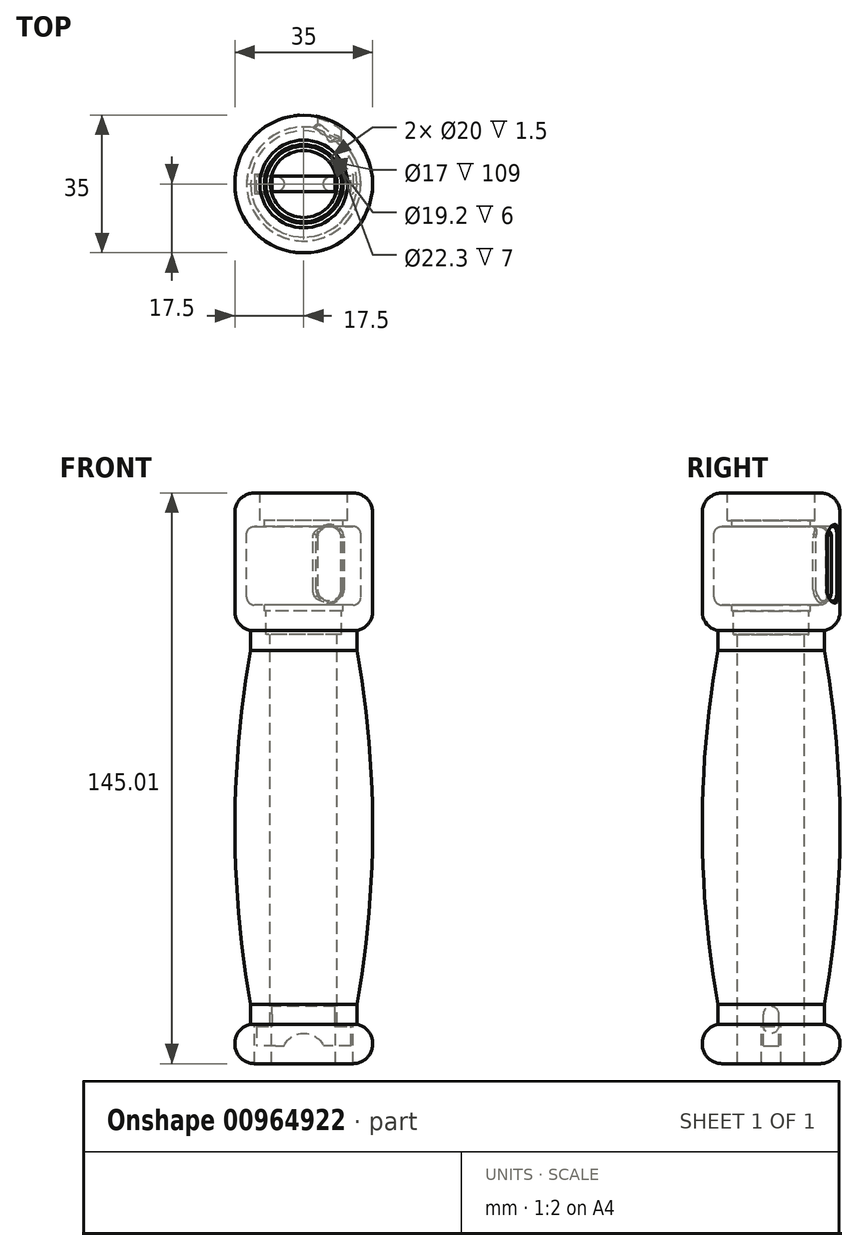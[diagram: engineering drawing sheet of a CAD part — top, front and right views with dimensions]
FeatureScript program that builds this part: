
annotation { "Feature Type Name" : "Feature", "Feature Type Description" : "" }
export const myFeature = defineFeature(function(context is Context, id is Id, definition is map)
    precondition{}
    {
        {
            var Q0;
            Q0=qCreatedBy(makeId("Front.planeOp"),FACE);
            var sketch = newSketch(context, id + "F0", { "sketchPlane" : qUnion([Q0])});
            skLineSegment(sketch, "E0", {"start": v(0, 0) * mm, "end": v(0, -145) * mm, "construction": true});
            skLineSegment(sketch, "E1", {"start": v(-17.5, 0) * mm, "end": v(-17.5, -35) * mm});
            skLineSegment(sketch, "E2", {"start": v(-17.5, -35) * mm, "end": v(-13.5, -35) * mm});
            skLineSegment(sketch, "E3", {"start": v(-13.5, -35) * mm, "end": v(-13.5, -40) * mm});
            skLineSegment(sketch, "E4", {"start": v(-13.5, -135) * mm, "end": v(-17.5, -135) * mm});
            skLineSegment(sketch, "E5", {"start": v(-17.5, -135) * mm, "end": v(-17.5, -145) * mm});
            skLineSegment(sketch, "E6", {"start": v(-17.5, 0) * mm, "end": v(-11.15, 0) * mm});
            skLineSegment(sketch, "E7", {"start": v(-11.15, 0) * mm, "end": v(0, 0) * mm, "construction": true});
            skLineSegment(sketch, "E8", {"start": v(-11.15, 0) * mm, "end": v(-11.15, -7) * mm});
            skLineSegment(sketch, "E9", {"start": v(-11.15, -7) * mm, "end": v(-10, -7) * mm});
            skLineSegment(sketch, "E10", {"start": v(-10, -7) * mm, "end": v(-10, -8.5) * mm});
            skLineSegment(sketch, "E11", {"start": v(-10, -30) * mm, "end": v(-9.6, -30) * mm});
            skLineSegment(sketch, "E12", {"start": v(-9.6, -30) * mm, "end": v(-9.6, -36) * mm});
            skLineSegment(sketch, "E13", {"start": v(-9.6, -36) * mm, "end": v(-8.5, -36) * mm});
            skLineSegment(sketch, "E14", {"start": v(-8.5, -36) * mm, "end": v(-8.5, -145) * mm});
            skLineSegment(sketch, "E15", {"start": v(-17.5, -145) * mm, "end": v(-8.5, -145) * mm});
            skLineSegment(sketch, "E16", {"start": v(-8.5, -145) * mm, "end": v(0, -145) * mm, "construction": true});
            skArc(sketch, "E17", {"start": v(-13.5, -40) * mm, "mid": v(-17.5, -85) * mm, "end": v(-13.5, -130) * mm});
            skLineSegment(sketch, "E18.trimOffspring", {"start": v(-13.5, -130) * mm, "end": v(-13.5, -135) * mm});
            skLineSegment(sketch, "E19", {"start": v(-13.5, -130) * mm, "end": v(-13.5, -40) * mm, "construction": true});
            skLineSegment(sketch, "E20", {"start": v(-10, -8.5) * mm, "end": v(-12.5, -8.5) * mm});
            skLineSegment(sketch, "E21", {"start": v(-14.5, -10.5) * mm, "end": v(-14.5, -26.5) * mm});
            skLineSegment(sketch, "E22", {"start": v(-12.5, -28.5) * mm, "end": v(-10, -28.5) * mm});
            skLineSegment(sketch, "E23.trimOffspring", {"start": v(-10, -28.5) * mm, "end": v(-10, -30) * mm});
            skPoint(sketch, "E24.visualSharp", {"position": v(-14.5, -8.5) * mm});
            skArc(sketch, "E24.filletArc", {"start": v(-12.5, -8.5) * mm, "mid": v(-13.91, -9.09) * mm, "end": v(-14.5, -10.5) * mm});
            skPoint(sketch, "E25.visualSharp", {"position": v(-14.5, -28.5) * mm});
            skArc(sketch, "E25.filletArc", {"start": v(-14.5, -26.5) * mm, "mid": v(-13.91, -27.91) * mm, "end": v(-12.5, -28.5) * mm});
            skSolve(sketch);
        }
        {
            var Q0;
            Q0 = qSketchRegion(id + "F0", true);
            var Q1;
            Q1=sQuery(id+"F0.wireOp",EDGE,"E0");
            revolve(context, id + "F1", {"surfaceOperationType" : NewSurfaceOperationType.NEW, "entities" : qUnion([Q0]), "axis" : qUnion([Q1]), "revolveType" : RevolveType.FULL});
        }
        {
            var Q0;
            Q0=qCreatedBy(makeId("Front.planeOp"),FACE);
            var sketch = newSketch(context, id + "F2", { "sketchPlane" : qUnion([Q0])});
            skLineSegment(sketch, "E26", {"start": v(0, 0) * mm, "end": v(0, -17) * mm, "construction": true});
            skLineSegment(sketch, "E27", {"start": v(6.5, -11.5) * mm, "end": v(6.5, -24.5) * mm, "construction": true});
            skLineSegment(sketch, "E28.0", {"start": v(3.5, -11.5) * mm, "end": v(3.5, -24.5) * mm});
            skLineSegment(sketch, "E29.0", {"start": v(9.5, -11.5) * mm, "end": v(9.5, -24.5) * mm});
            skArc(sketch, "E30", {"start": v(9.5, -11.5) * mm, "mid": v(6.5, -8.5) * mm, "end": v(3.5, -11.5) * mm});
            skArc(sketch, "E31", {"start": v(3.5, -24.5) * mm, "mid": v(6.5, -27.5) * mm, "end": v(9.5, -24.5) * mm});
            skSolve(sketch);
        }
        {
            var Q0;
            Q0 = qSketchRegion(id + "F2", true);
            var Q1;
            Q1=makeQuery(id+"F1.opRevolve","SWEPT_FACE",FACE,{"disambiguationData":[OSD([sQuery(id+"F0.wireOp",EDGE,"E17")])]});
            extrude(context, id + "F3", {"entities" : qUnion([Q0]), "operationType" : NewBodyOperationType.REMOVE, "oppositeDirection" : true, "depth" : 25 * mm, "endBoundEntityFace" : qUnion([Q1]), "offsetDistance" : 25 * mm});
        }
        {
            var Q0;
            Q0=makeQuery(id+"FU2xquRf8RpkaLV_1.boolean.opBoolean","INTERSECT",EDGE,{"derivedFrom":[makeQuery(id+"F3.boolean.opBoolean","COPY",FACE,{"derivedFrom":makeQuery(id+"F3.opExtrude","SWEPT_FACE",FACE,{"disambiguationData":[OSD([sQuery(id+"F2.wireOp",EDGE,"E29.0")])]})}),makeQuery(id+"FU2xquRf8RpkaLV_1.opExtrude","SWEPT_FACE",FACE,{"disambiguationData":[OSD([sQuery(id+"F2XugFDrMGOCg4c_1.wireOp",EDGE,"g1a4RwnO-Dt7v-LiwX-xQ2X-J9SUyvn5bniC")])]})]});
            var Q1;
            Q1=makeQuery(id+"F3.boolean.opBoolean","INTERSECT",EDGE,{"derivedFrom":[makeQuery(id+"F1.opRevolve","SWEPT_FACE",FACE,{"disambiguationData":[OSD([sQuery(id+"F0.wireOp",EDGE,"E1")])]}),makeQuery(id+"F3.opExtrude","SWEPT_FACE",FACE,{"disambiguationData":[OSD([sQuery(id+"F2.wireOp",EDGE,"E29.0")])]})]});
            chamfer(context, id + "F4", {"entities" : qUnion([Q0, Q1]), "width" : .5 * mm, "tangentPropagation" : true});
        }
        {
            var Q0;
            Q0=makeQuery(id+"F1.opRevolve","SWEPT_EDGE",EDGE,{"disambiguationData":[OSD([sQuery(id+"F0.wireOp",EDGE,"E1"),sQuery(id+"F0.wireOp",EDGE,"E6")])]});
            var Q1;
            Q1=makeQuery(id+"F1.opRevolve","SWEPT_EDGE",EDGE,{"disambiguationData":[OSD([sQuery(id+"F0.wireOp",EDGE,"E1"),sQuery(id+"F0.wireOp",EDGE,"E2")])]});
            var Q2;
            Q2=makeQuery(id+"F1.opRevolve","SWEPT_EDGE",EDGE,{"disambiguationData":[OSD([sQuery(id+"F0.wireOp",EDGE,"E4"),sQuery(id+"F0.wireOp",EDGE,"E5")])]});
            var Q3;
            Q3=makeQuery(id+"F1.opRevolve","SWEPT_EDGE",EDGE,{"disambiguationData":[OSD([sQuery(id+"F0.wireOp",EDGE,"E5"),sQuery(id+"F0.wireOp",EDGE,"E15")])]});
            fillet(context, id + "F5", {"entities" : qUnion([Q0, Q1, Q2, Q3]), "radius" : 5 * mm, "tangentPropagation" : true, "allowEdgeOverflow" : false});
        }
        {
            var Q0;
            Q0=qCreatedBy(makeId("Right.planeOp"),FACE);
            var sketch = newSketch(context, id + "F6", { "sketchPlane" : qUnion([Q0])});
            skLineSegment(sketch, "E32", {"start": v(0, 0) * mm, "end": v(0, -145) * mm, "construction": true});
            skLineSegment(sketch, "E33", {"start": v(0, -145) * mm, "end": v(-2.5, -145) * mm});
            skLineSegment(sketch, "E34", {"start": v(-2.5, -145) * mm, "end": v(-2.5, -135) * mm});
            skLineSegment(sketch, "E35", {"start": v(-2.5, -135) * mm, "end": v(0, -135) * mm});
            skLineSegment(sketch, "E36.MirrorCS", {"start": v(2.5, -135) * mm, "end": v(0, -135) * mm});
            skLineSegment(sketch, "E37.MirrorCS", {"start": v(2.5, -145) * mm, "end": v(2.5, -135) * mm});
            skLineSegment(sketch, "E38.MirrorCS", {"start": v(0, -145) * mm, "end": v(2.5, -145) * mm});
            skSolve(sketch);
        }
        {
            var Q0;
            Q0 = qSketchRegion(id + "F6", true);
            extrude(context, id + "F7", {"entities" : qUnion([Q0]), "operationType" : NewBodyOperationType.REMOVE, "endBound" : BoundingType.SYMMETRIC, "oppositeDirection" : true, "depth" : 25 * mm, "offsetDistance" : 25 * mm});
        }
        {
            var Q0;
            Q0=qCreatedBy(makeId("Front.planeOp"),FACE);
            var sketch = newSketch(context, id + "F8", { "sketchPlane" : qUnion([Q0])});
            skLineSegment(sketch, "E39", {"start": v(0, 0) * mm, "end": v(0, -145) * mm, "construction": true});
            skLineSegment(sketch, "E40", {"start": v(12, -140.5) * mm, "end": v(12, -135.5) * mm});
            skLineSegment(sketch, "E41", {"start": v(8, -135.5) * mm, "end": v(12, -135.5) * mm});
            skLineSegment(sketch, "E42", {"start": v(8, -135.5) * mm, "end": v(8, -130.5) * mm});
            skLineSegment(sketch, "E43", {"start": v(8, -130.5) * mm, "end": v(-8, -130.5) * mm});
            skLineSegment(sketch, "E44", {"start": v(-8, -130.5) * mm, "end": v(-8, -135.5) * mm});
            skLineSegment(sketch, "E45", {"start": v(-12, -135.5) * mm, "end": v(-8, -135.5) * mm});
            skLineSegment(sketch, "E46", {"start": v(-12, -135.5) * mm, "end": v(-12, -140.5) * mm});
            skLineSegment(sketch, "E47", {"start": v(12, -140.5) * mm, "end": v(5, -140.5) * mm});
            skPoint(sketch, "E48.orphan", {"position": v(-12, -145) * mm});
            skArc(sketch, "E49", {"start": v(5, -140.5) * mm, "mid": v(0, -137.3) * mm, "end": v(-5, -140.5) * mm});
            skLineSegment(sketch, "E50.trimOffspring", {"start": v(-5, -140.5) * mm, "end": v(-12, -140.5) * mm});
            skSolve(sketch);
        }
        {
            var Q0;
            Q0 = qSketchRegion(id + "F8", true);
            extrude(context, id + "F9", {"entities" : qUnion([Q0]), "operationType" : NewBodyOperationType.ADD, "endBound" : BoundingType.SYMMETRIC, "depth" : 4 * mm, "offsetDistance" : 25 * mm});
        }
        {
            var Q0;
            Q0=makeQuery(id+"F3.boolean.opBoolean","INTERSECT",EDGE,{"derivedFrom":[makeQuery(id+"F1.opRevolve","SWEPT_FACE",FACE,{"disambiguationData":[OSD([sQuery(id+"F0.wireOp",EDGE,"E21")])]}),makeQuery(id+"F3.opExtrude","SWEPT_FACE",FACE,{"disambiguationData":[OSD([sQuery(id+"F2.wireOp",EDGE,"E29.0")])]})]});
            chamfer(context, id + "F10", {"entities" : qUnion([Q0]), "width" : 1 * mm, "tangentPropagation" : true});
        }
        {
            var Q0;
            Q0=makeQuery(id+"F9.opExtrude","CAP_EDGE",EDGE,{"disambiguationData":[OSD([sQuery(id+"F8.wireOp",EDGE,"E49")])],"isStart":false});
            var Q1;
            Q1=makeQuery(id+"F9.opExtrude","CAP_EDGE",EDGE,{"disambiguationData":[OSD([sQuery(id+"F8.wireOp",EDGE,"E49")])],"isStart":true});
            var Q2;
            Q2=makeQuery(id+"F9.opExtrude","CAP_EDGE",EDGE,{"disambiguationData":[OSD([sQuery(id+"F8.wireOp",EDGE,"E43")])],"isStart":true});
            var Q3;
            Q3=makeQuery(id+"F9.opExtrude","CAP_EDGE",EDGE,{"disambiguationData":[OSD([sQuery(id+"F8.wireOp",EDGE,"E43")])],"isStart":false});
            fillet(context, id + "F11", {"entities" : qUnion([Q0, Q1, Q2, Q3]), "radius" : 2 * mm, "tangentPropagation" : true, "allowEdgeOverflow" : false});
        }
    });
